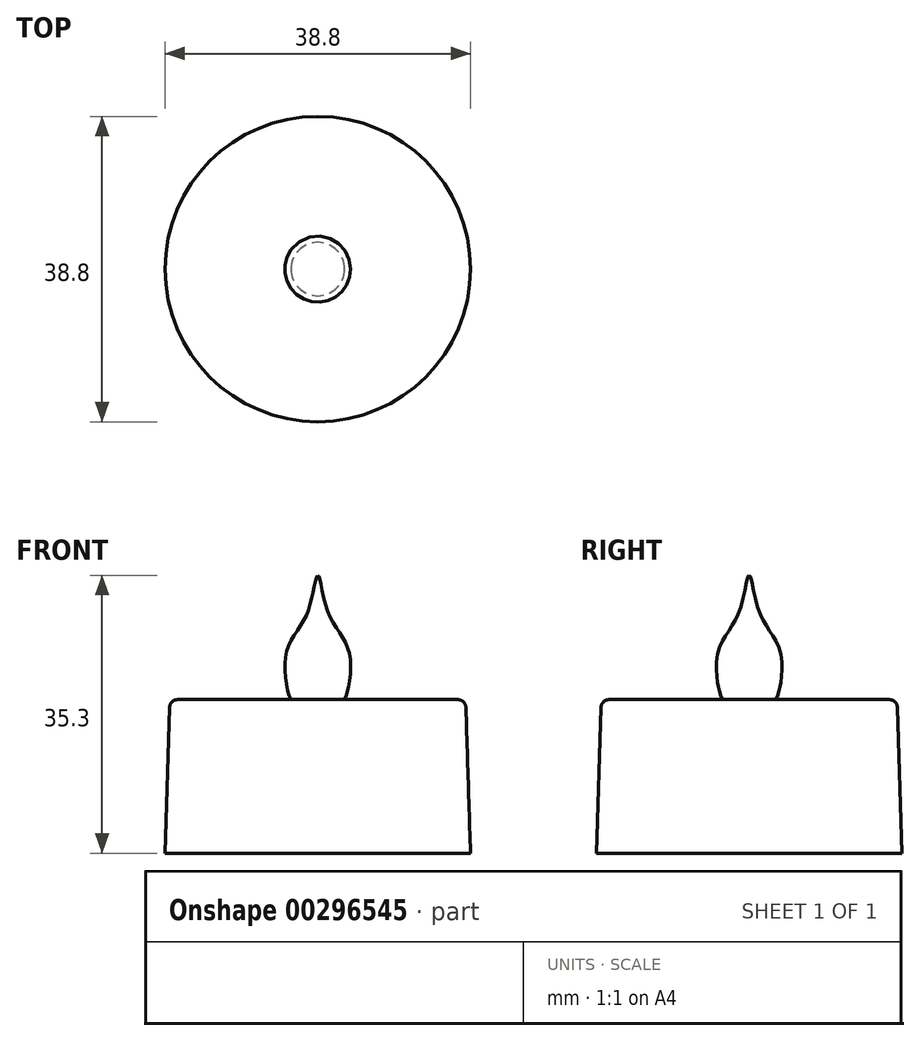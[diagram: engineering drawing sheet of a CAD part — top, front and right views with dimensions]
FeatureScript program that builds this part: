
annotation { "Feature Type Name" : "Feature", "Feature Type Description" : "" }
export const myFeature = defineFeature(function(context is Context, id is Id, definition is map)
    precondition{}
    {
        {
            var Q0;
            Q0=qCreatedBy(makeId("Top.planeOp"),FACE);
            var sketch = newSketch(context, id + "F0", { "sketchPlane" : qUnion([Q0]), "disableImprinting" : false});
            skCircle(sketch, "E0", {"center": v(0, 0) * mm, "radius": 19.4 * mm});
            skSolve(sketch);
        }
        {
            var Q0;
            Q0 = qSketchRegion(id + "F0", true);
            extrude(context, id + "F1", {"entities" : qUnion([Q0]), "depth" : 19.5 * mm, "hasDraft" : true, "draftAngle" : 1.8 * degree, "draftPullDirection" : true});
        }
        {
            var Q0;
            Q0=makeQuery(id+"F1.opExtrude","CAP_FACE",FACE,{"disambiguationData":[OSD([sQuery(id+"F0.wireOp",EDGE,"E0")])],"isStart":false});
            fillet(context, id + "F2", {"entities" : qUnion([Q0]), "radius" : 1 * mm, "tangentPropagation" : true, "allowEdgeOverflow" : false});
        }
        {
            var Q0;
            Q0=qCreatedBy(makeId("Front.planeOp"),FACE);
            var sketch = newSketch(context, id + "F3", { "sketchPlane" : qUnion([Q0])});
            skLineSegment(sketch, "E1.0", {"start": v(-17.82, 19.5) * mm, "end": v(17.82, 19.5) * mm});
            skLineSegment(sketch, "E2", {"start": v(0, 19.5) * mm, "end": v(0, 35.3) * mm});
            skPoint(sketch, "E2.endSnap0", {"position": v(0, 19.5) * mm});
            skFitSpline(sketch, "E3", {"points": [v(0, 35.3) * mm, v(1.29, 30.62) * mm, v(4.06, 25.2) * mm, v(3.4, 19.5) * mm], "startDerivative": vector(3.38, 0) * mm, "endDerivative": vector(-3.64, -5.52) * mm});
            skSolve(sketch);
        }
        {
            var Q0;
            Q0 = qSketchRegion(id + "F3", true);
            var Q1;
            Q1=sQuery(id+"F3.wireOp",EDGE,"E2");
            revolve(context, id + "F4", {"entities" : qUnion([Q0]), "axis" : qUnion([Q1]), "revolveType" : RevolveType.FULL});
        }
    });
